# Revit family: Legrand_Tableautin_épaisseur_70mm
name_source: partatom
category: Equipement électrique
revit_build: Autodesk Revit 2018 (Build: 20170223_1515(x64)
units: mm (PartAtom-declared; Revit-internal decimal feet)

## family parameters
Basée sur le plan de construction = Non
Configuration du panneau = Deux colonnes, circuits au sein
Cote de connecteur circulaire = Utiliser le diamètre
Couper avec des vides une fois chargée = Non
Numéro OmniClass = 23.80.30.11.17
Partagée = Non
Point de calcul de pièce = Non
Titre OmniClass = Distribution Boards and Control Panels
Toujours verticalement = Oui
Type d'élément = Tableau de raccordement

## types (3) — shared parameters
Conditions Générale d'Utilisation = https://export.legrand.com
ETIM Class 6.0 = EC000214
Epaisseur = 70mm
Fabricant = Legrand
IK = 08
IP = 20
Image du type = <Aucun>
Matière = Polystyrène
Polystyrène
RAL = 9003
URL = www.legrand.fr

## per-type parameters (varying)
| type | Hauteur | Largeur | Tableautin 039141 | Tableautin 039142 | Tableautin 039145 |
| Tableautin 039141 | 250mm | 150mm | Oui | Non | Non |
| Tableautin 039142 | 300mm | 250mm | Non | Oui | Non |
| Tableautin 039145 | 500mm | 300mm | Non | Non | Oui |

note: column(s) folded — value = type name in every type: Description
